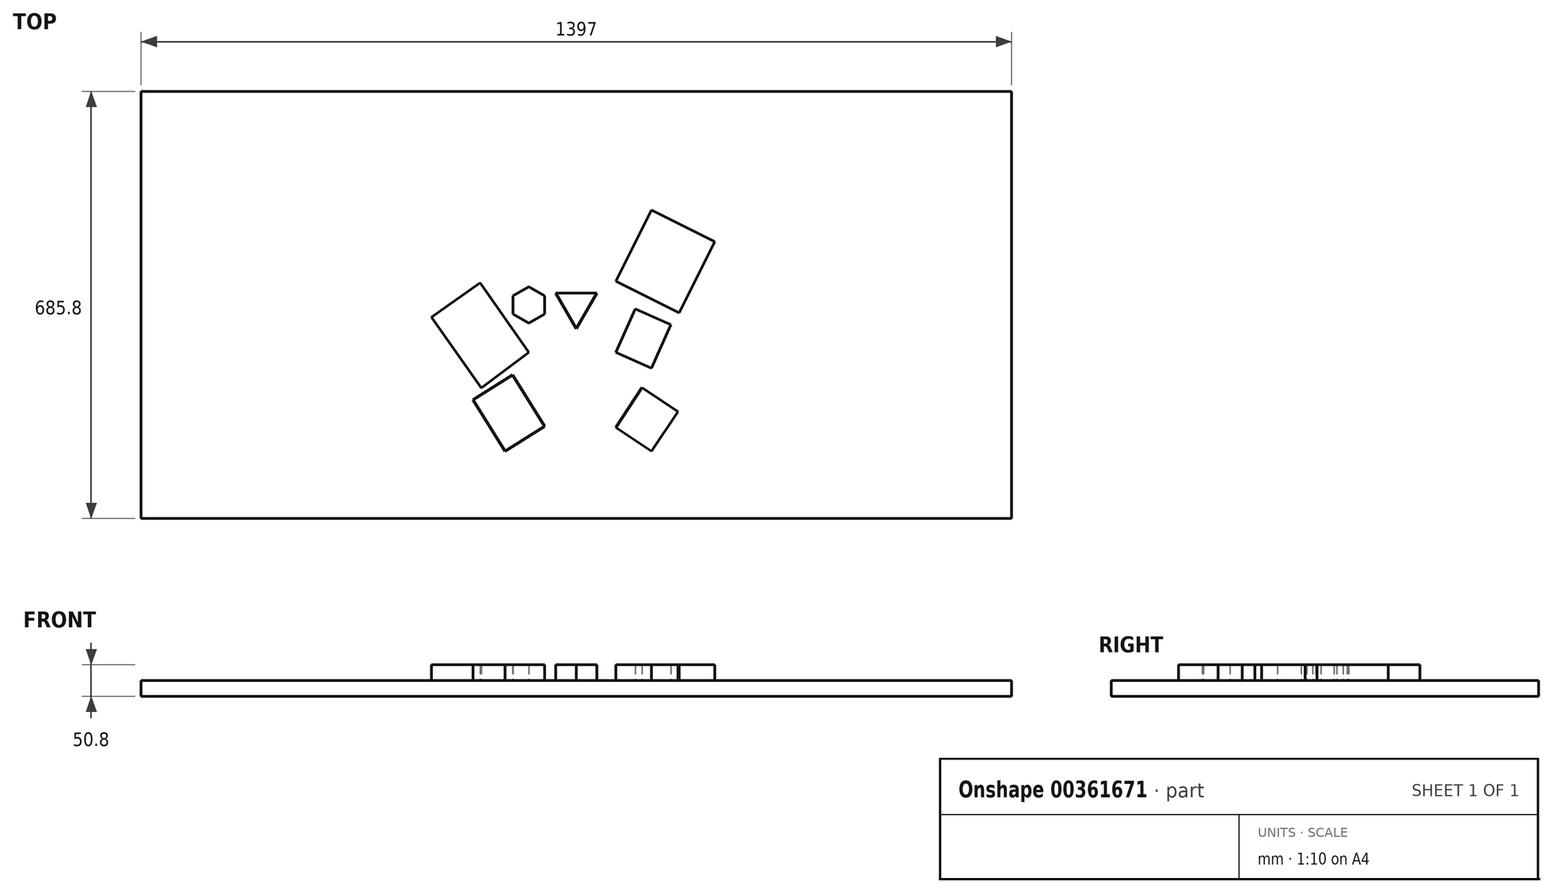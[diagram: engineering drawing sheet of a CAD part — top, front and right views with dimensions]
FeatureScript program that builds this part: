
annotation { "Feature Type Name" : "Feature", "Feature Type Description" : "" }
export const myFeature = defineFeature(function(context is Context, id is Id, definition is map)
    precondition{}
    {
        {
            var Q0;
            Q0=qCreatedBy(makeId("Top.planeOp"),FACE);
            var sketch = newSketch(context, id + "F0", { "sketchPlane" : qUnion([Q0])});
            skLineSegment(sketch, "E0.bottom", {"start": v(698.5, -342.9) * mm, "end": v(-698.5, -342.9) * mm});
            skLineSegment(sketch, "E0.top", {"start": v(698.5, 342.9) * mm, "end": v(-698.5, 342.9) * mm});
            skLineSegment(sketch, "E0.left", {"start": v(698.5, -342.9) * mm, "end": v(698.5, 342.9) * mm});
            skLineSegment(sketch, "E0.right", {"start": v(-698.5, -342.9) * mm, "end": v(-698.5, 342.9) * mm});
            skPoint(sketch, "E0.middle", {"position": v(0, 0) * mm});
            skSolve(sketch);
        }
        {
            var Q0;
            Q0 = qSketchRegion(id + "F0", true);
            extrude(context, id + "F1", {"entities" : qUnion([Q0]), "depth" : 25.4 * mm});
        }
        {
            var Q0;
            Q0=makeQuery(id+"F1.opExtrude","CAP_FACE",FACE,{"disambiguationData":[OSD([sQuery(id+"F0.wireOp",EDGE,"E0.bottom"),sQuery(id+"F0.wireOp",EDGE,"E0.top"),sQuery(id+"F0.wireOp",EDGE,"E0.left"),sQuery(id+"F0.wireOp",EDGE,"E0.right")])],"isStart":false});
            var sketch = newSketch(context, id + "F2", { "sketchPlane" : qUnion([Q0])});
            skLineSegment(sketch, "E1.bottom", {"start": v(63.5, -50.8) * mm, "end": v(-57.15, -50.8) * mm, "construction": true});
            skLineSegment(sketch, "E1.top", {"start": v(63.5, -152.4) * mm, "end": v(-57.15, -152.4) * mm, "construction": true});
            skLineSegment(sketch, "E1.left", {"start": v(63.5, -50.8) * mm, "end": v(63.5, -149.49) * mm, "construction": true});
            skLineSegment(sketch, "E1.right", {"start": v(-57.15, -50.8) * mm, "end": v(-57.15, -152.4) * mm, "construction": true});
            skPoint(sketch, "E1.middle", {"position": v(3.17, -101.6) * mm});
            skLineSegment(sketch, "E2.MirrorCS", {"start": v(-152.4, -133.35) * mm, "end": v(-76.2, -76.2) * mm});
            skLineSegment(sketch, "E3.MirrorCS", {"start": v(-152.4, -133.35) * mm, "end": v(-232.4, -19.96) * mm});
            skLineSegment(sketch, "E4.MirrorCS", {"start": v(-232.4, -19.96) * mm, "end": v(-154.27, 35.17) * mm});
            skPoint(sketch, "E5.MirrorP", {"position": v(-154.49, -44.3) * mm});
            skLineSegment(sketch, "E6.top", {"start": v(162.98, -171.45) * mm, "end": v(105.28, -132.98) * mm});
            skLineSegment(sketch, "E6.left", {"start": v(120.65, -234.95) * mm, "end": v(162.98, -171.45) * mm});
            skPoint(sketch, "E6.middle", {"position": v(112.96, -183.97) * mm});
            skCircle(sketch, "E7.cCircle", {"center": v(0, 0) * mm, "radius": 19.05 * mm, "construction": true});
            skLineSegment(sketch, "E7.0", {"start": v(33, 19.05) * mm, "end": v(0, -38.1) * mm});
            skLineSegment(sketch, "E7.1", {"start": v(0, -38.1) * mm, "end": v(-33, 19.05) * mm});
            skLineSegment(sketch, "E7.2", {"start": v(-33, 19.05) * mm, "end": v(33, 19.05) * mm});
            skCircle(sketch, "E8.cCircle", {"center": v(-76.2, 0) * mm, "radius": 25.4 * mm, "construction": true});
            skLineSegment(sketch, "E8.0", {"start": v(-50.8, 14.66) * mm, "end": v(-50.8, -14.66) * mm});
            skLineSegment(sketch, "E8.1", {"start": v(-50.8, -14.66) * mm, "end": v(-76.2, -29.33) * mm});
            skLineSegment(sketch, "E8.2", {"start": v(-76.2, -29.33) * mm, "end": v(-101.6, -14.66) * mm});
            skLineSegment(sketch, "E8.3", {"start": v(-101.6, -14.66) * mm, "end": v(-101.6, 14.66) * mm});
            skLineSegment(sketch, "E8.4", {"start": v(-101.6, 14.66) * mm, "end": v(-76.2, 29.33) * mm});
            skLineSegment(sketch, "E8.5", {"start": v(-76.2, 29.33) * mm, "end": v(-50.8, 14.66) * mm});
            skPoint(sketch, "E8.0.midPoint", {"position": v(-50.8, 0) * mm});
            skLineSegment(sketch, "E9.bottom", {"start": v(120.65, -101.6) * mm, "end": v(63.5, -76.2) * mm});
            skLineSegment(sketch, "E9.top", {"start": v(151.6, -31.97) * mm, "end": v(94.45, -6.57) * mm});
            skLineSegment(sketch, "E9.left", {"start": v(120.65, -101.6) * mm, "end": v(151.6, -31.97) * mm});
            skLineSegment(sketch, "E9.right", {"start": v(63.5, -76.2) * mm, "end": v(94.45, -6.57) * mm});
            skPoint(sketch, "E9.middle", {"position": v(107.55, -54.08) * mm});
            skLineSegment(sketch, "E10.bottom", {"start": v(165.1, -12.7) * mm, "end": v(63.5, 38.1) * mm});
            skLineSegment(sketch, "E10.top", {"start": v(222.12, 101.35) * mm, "end": v(120.52, 152.15) * mm});
            skLineSegment(sketch, "E10.left", {"start": v(165.1, -12.7) * mm, "end": v(222.12, 101.35) * mm});
            skLineSegment(sketch, "E10.right", {"start": v(63.5, 38.1) * mm, "end": v(120.52, 152.15) * mm});
            skPoint(sketch, "E10.middle", {"position": v(142.81, 69.72) * mm});
            skLineSegment(sketch, "E11.bottom", {"start": v(-50.8, -195.24) * mm, "end": v(-114.3, -234.95) * mm});
            skLineSegment(sketch, "E11.top", {"start": v(-102.49, -112.59) * mm, "end": v(-165.99, -152.3) * mm});
            skLineSegment(sketch, "E11.left", {"start": v(-50.8, -195.24) * mm, "end": v(-102.49, -112.59) * mm});
            skLineSegment(sketch, "E11.right", {"start": v(-114.3, -234.95) * mm, "end": v(-165.99, -152.3) * mm});
            skPoint(sketch, "E11.middle", {"position": v(-108.4, -173.77) * mm});
            skPoint(sketch, "E12", {"position": v(-114.3, -104.77) * mm});
            skLineSegment(sketch, "E13", {"start": v(63.5, -149.49) * mm, "end": v(63.5, -149.85) * mm, "construction": true});
            skLineSegment(sketch, "E14", {"start": v(120.65, -234.95) * mm, "end": v(63.5, -196.85) * mm});
            skLineSegment(sketch, "E15", {"start": v(63.5, -196.85) * mm, "end": v(105.28, -132.98) * mm});
            skLineSegment(sketch, "E16", {"start": v(-154.27, 35.17) * mm, "end": v(-76.2, -76.2) * mm});
            skSolve(sketch);
        }
        {
            var Q0;
            Q0 = qSketchRegion(id + "F2", true);
            extrude(context, id + "F3", {"entities" : qUnion([Q0]), "depth" : 25.4 * mm});
        }
    });
